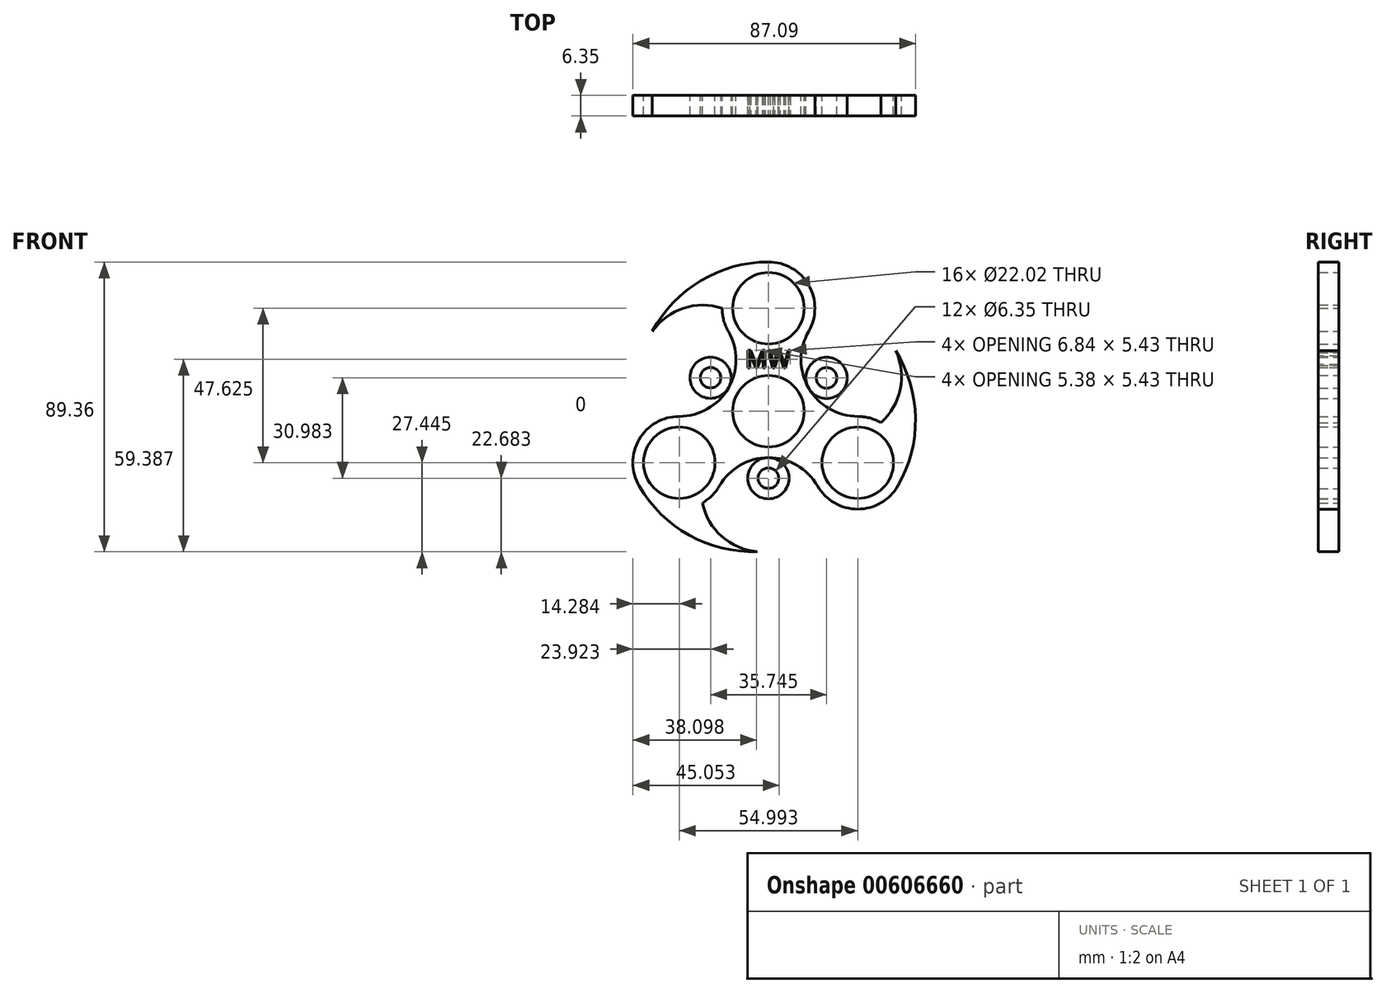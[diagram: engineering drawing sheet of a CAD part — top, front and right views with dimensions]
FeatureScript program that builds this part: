
annotation { "Feature Type Name" : "Feature", "Feature Type Description" : "" }
export const myFeature = defineFeature(function(context is Context, id is Id, definition is map)
    precondition{}
    {
        {
            var Q0;
            Q0=qCreatedBy(makeId("Front.planeOp"),FACE);
            var sketch = newSketch(context, id + "F0", { "sketchPlane" : qUnion([Q0])});
            skCircle(sketch, "E0", {"center": v(0, 31.75) * mm, "radius": 14.29 * mm});
            skCircle(sketch, "E1", {"center": v(0, 31.75) * mm, "radius": 11.01 * mm});
            skCircle(sketch, "E2", {"center": v(0, 0) * mm, "radius": 14.29 * mm});
            skCircle(sketch, "E3", {"center": v(0, 0) * mm, "radius": 11.01 * mm});
            skCircle(sketch, "E4.1.0", {"center": v(-27.5, -15.87) * mm, "radius": 11.01 * mm});
            skCircle(sketch, "E4.1.1", {"center": v(-27.5, -15.87) * mm, "radius": 14.29 * mm});
            skCircle(sketch, "E4.2.0", {"center": v(27.5, -15.88) * mm, "radius": 11.01 * mm});
            skCircle(sketch, "E4.2.1", {"center": v(27.5, -15.88) * mm, "radius": 14.29 * mm});
            skArc(sketch, "E5", {"start": v(-27.5, -1.59) * mm, "mid": v(-12.37, 7.14) * mm, "end": v(-12.37, 24.6) * mm});
            skArc(sketch, "E6.1.0", {"start": v(15.12, -23.02) * mm, "mid": v(0, -14.29) * mm, "end": v(-15.12, -23.02) * mm});
            skArc(sketch, "E6.2.0", {"start": v(12.37, 24.6) * mm, "mid": v(12.37, 7.14) * mm, "end": v(27.5, -1.59) * mm});
            skArc(sketch, "E7", {"start": v(0, 46.04) * mm, "mid": v(-20.86, 40.27) * mm, "end": v(-35.79, 24.6) * mm});
            skArc(sketch, "E8", {"start": v(-14.29, 31.75) * mm, "mid": v(-26.23, 31.76) * mm, "end": v(-35.79, 24.6) * mm});
            skArc(sketch, "E9.1.0", {"start": v(-20.35, -28.25) * mm, "mid": v(-14.39, -38.6) * mm, "end": v(-3.42, -43.3) * mm});
            skArc(sketch, "E9.1.1", {"start": v(-39.87, -23.02) * mm, "mid": v(-24.45, -38.2) * mm, "end": v(-3.42, -43.3) * mm});
            skArc(sketch, "E9.2.0", {"start": v(34.64, -3.5) * mm, "mid": v(40.62, 6.83) * mm, "end": v(39.2, 18.69) * mm});
            skArc(sketch, "E9.2.1", {"start": v(39.87, -23.02) * mm, "mid": v(45.3, -2.07) * mm, "end": v(39.2, 18.69) * mm});
            skCircle(sketch, "E10", {"center": v(-17.86, 10.35) * mm, "radius": 6.35 * mm});
            skCircle(sketch, "E11", {"center": v(-17.86, 10.35) * mm, "radius": 3.18 * mm});
            skCircle(sketch, "E12.1.0", {"center": v(-0.03, -20.64) * mm, "radius": 6.35 * mm});
            skCircle(sketch, "E12.1.1", {"center": v(-0.03, -20.64) * mm, "radius": 3.18 * mm});
            skCircle(sketch, "E12.2.0", {"center": v(17.89, 10.3) * mm, "radius": 6.35 * mm});
            skCircle(sketch, "E12.2.1", {"center": v(17.89, 10.3) * mm, "radius": 3.18 * mm});
            skSolve(sketch);
        }
        {
            var Q0;
            Q0 = qSketchRegion(id + "F0", true);
            extrude(context, id + "F1", {"entities" : qUnion([Q0]), "depth" : 6.35 * mm, "offsetDistance" : 25.4 * mm});
        }
        {
            var Q0;
            Q0=makeQuery(id+"F1.opExtrude","CAP_FACE",FACE,{"disambiguationData":[OSD([sQuery(id+"F0.wireOp",EDGE,"E0"),sQuery(id+"F0.wireOp",EDGE,"E1"),sQuery(id+"F0.wireOp",EDGE,"E3"),sQuery(id+"F0.wireOp",EDGE,"E4.1.0"),sQuery(id+"F0.wireOp",EDGE,"E4.1.1"),sQuery(id+"F0.wireOp",EDGE,"E4.2.0"),sQuery(id+"F0.wireOp",EDGE,"E4.2.1"),sQuery(id+"F0.wireOp",EDGE,"E5"),sQuery(id+"F0.wireOp",EDGE,"E6.1.0"),sQuery(id+"F0.wireOp",EDGE,"E6.2.0"),sQuery(id+"F0.wireOp",EDGE,"E7"),sQuery(id+"F0.wireOp",EDGE,"E8"),sQuery(id+"F0.wireOp",EDGE,"E9.1.0"),sQuery(id+"F0.wireOp",EDGE,"E9.1.1"),sQuery(id+"F0.wireOp",EDGE,"E9.2.0"),sQuery(id+"F0.wireOp",EDGE,"E9.2.1")])],"isStart":false});
            var sketch = newSketch(context, id + "F2", { "sketchPlane" : qUnion([Q0])});
            skText(sketch, "E13", { "text": "MW", "fontName": "OpenSans-Regular.ttf"});
            const initialGuessF2  = {"E13": [-0.00712, 0.01335, 1, 0, 0.00548]};
            skSetInitialGuess(sketch, initialGuessF2);
            skSolve(sketch);
        }
        {
            var Q0;
            Q0 = qSketchRegion(id + "F2", true);
            extrude(context, id + "F3", {"entities" : qUnion([Q0]), "operationType" : NewBodyOperationType.REMOVE, "endBound" : BoundingType.THROUGH_ALL, "oppositeDirection" : true, "depth" : 25.4 * mm, "offsetDistance" : 25.4 * mm});
        }
    });
